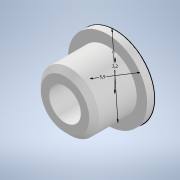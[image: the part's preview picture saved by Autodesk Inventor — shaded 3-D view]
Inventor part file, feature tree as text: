
AUTODESK INVENTOR PART (.ipt)
format: ipt  version: 2022 (Build 260153000, 153)  size: 125,440 bytes
history: native  units: mm
features: sketch x3, extrude x2, other x1, chamfer x1
ambient origin geometry x8: Origin, YZ Plane, XZ Plane, XY Plane, X Axis, Y Axis, Z Axis, Center Point
bodies: Body1 (feature_tree)
feature tree (7):
  other  "Твердое тело1"
  sketch  "Эскиз1"
  extrude  "Выдавливание1"  Depth=5.9mm
  extrude  "Выдавливание3"  Depth=3.2mm
  chamfer  "Фаска1"  Distance=8.0mm
  sketch  "Эскиз2"
  sketch  "Эскиз4"
